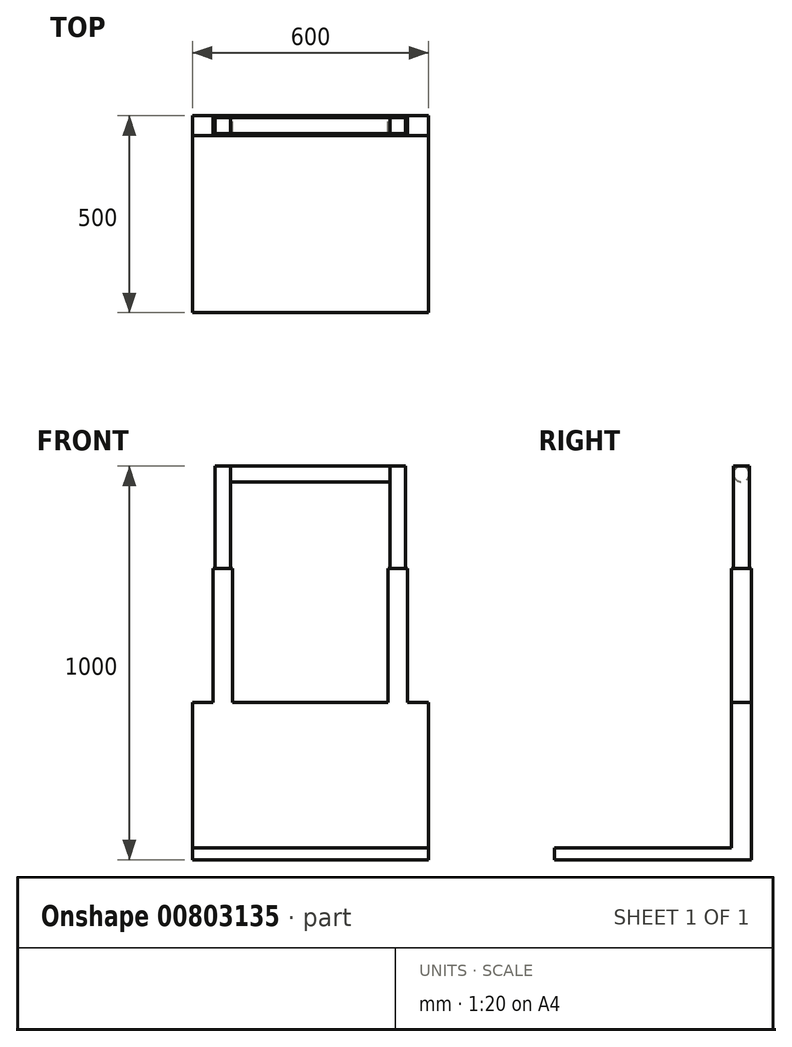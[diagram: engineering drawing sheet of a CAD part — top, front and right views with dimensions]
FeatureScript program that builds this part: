
annotation { "Feature Type Name" : "Feature", "Feature Type Description" : "" }
export const myFeature = defineFeature(function(context is Context, id is Id, definition is map)
    precondition{}
    {
        {
            var Q0;
            Q0=qCreatedBy(makeId("Right.planeOp"),FACE);
            var sketch = newSketch(context, id + "F0", { "sketchPlane" : qUnion([Q0])});
            skLineSegment(sketch, "E0.bottom", {"start": v(-3.33, 13.74) * mm, "end": v(496.67, 13.74) * mm});
            skLineSegment(sketch, "E0.top", {"start": v(-3.33, -16.26) * mm, "end": v(496.67, -16.26) * mm});
            skLineSegment(sketch, "E0.left", {"start": v(-3.33, 13.74) * mm, "end": v(-3.33, -16.26) * mm});
            skLineSegment(sketch, "E0.right", {"start": v(496.67, 13.74) * mm, "end": v(496.67, -16.26) * mm});
            skLineSegment(sketch, "E1.bottom", {"start": v(496.67, 13.74) * mm, "end": v(446.67, 13.74) * mm});
            skLineSegment(sketch, "E1.top", {"start": v(496.67, 383.74) * mm, "end": v(446.67, 383.74) * mm});
            skLineSegment(sketch, "E1.left", {"start": v(496.67, 13.74) * mm, "end": v(496.67, 383.74) * mm});
            skLineSegment(sketch, "E1.right", {"start": v(446.67, 13.74) * mm, "end": v(446.67, 383.74) * mm});
            skSolve(sketch);
        }
        {
            var Q0;
            Q0=makeQuery(id+"F0.imprint","IMPRINT",FACE,{"disambiguationData":[TD([[makeQuery(id+"F0.imprint","IMPRINT",EDGE,{"derivedFrom":sQuery(id+"F0.wireOp",EDGE,"E1.top")}),1.0]])]});
            var Q1;
            Q1=makeQuery(id+"F0.imprint","IMPRINT",FACE,{"disambiguationData":[TD([[makeQuery(id+"F0.imprint","IMPRINT",EDGE,{"derivedFrom":sQuery(id+"F0.wireOp",EDGE,"E0.top")}),1.0]])]});
            extrude(context, id + "F1", {"entities" : qUnion([Q0, Q1]), "oppositeDirection" : true, "depth" : 600 * mm, "offsetDistance" : 25 * mm});
        }
        {
            var Q0;
            Q0=makeQuery(id+"F1.opExtrude","SWEPT_FACE",FACE,{"disambiguationData":[OSD([sQuery(id+"F0.wireOp",EDGE,"E1.top")])]});
            var sketch = newSketch(context, id + "F2", { "sketchPlane" : qUnion([Q0])});
            skLineSegment(sketch, "E2.bottom", {"start": v(-547.25, 446.67) * mm, "end": v(-497.25, 446.67) * mm});
            skLineSegment(sketch, "E2.top", {"start": v(-547.25, 496.67) * mm, "end": v(-497.25, 496.67) * mm});
            skLineSegment(sketch, "E2.left", {"start": v(-547.25, 446.67) * mm, "end": v(-547.25, 496.67) * mm});
            skLineSegment(sketch, "E2.right", {"start": v(-497.25, 446.67) * mm, "end": v(-497.25, 496.67) * mm});
            skLineSegment(sketch, "E3.bottom", {"start": v(-542.25, 451.67) * mm, "end": v(-502.25, 451.67) * mm});
            skLineSegment(sketch, "E3.top", {"start": v(-542.25, 491.67) * mm, "end": v(-502.25, 491.67) * mm});
            skLineSegment(sketch, "E3.left", {"start": v(-542.25, 451.67) * mm, "end": v(-542.25, 491.67) * mm});
            skLineSegment(sketch, "E3.right", {"start": v(-502.25, 451.67) * mm, "end": v(-502.25, 491.67) * mm});
            skLineSegment(sketch, "E4", {"start": v(-300, 713.33) * mm, "end": v(-300, 248.48) * mm});
            skLineSegment(sketch, "E5.MirrorCS", {"start": v(-102.75, 446.67) * mm, "end": v(-102.75, 496.67) * mm});
            skLineSegment(sketch, "E6.MirrorCS", {"start": v(-52.75, 496.67) * mm, "end": v(-102.75, 496.67) * mm});
            skLineSegment(sketch, "E7.MirrorCS", {"start": v(-52.75, 446.67) * mm, "end": v(-52.75, 496.67) * mm});
            skLineSegment(sketch, "E8.MirrorCS", {"start": v(-52.75, 446.67) * mm, "end": v(-102.75, 446.67) * mm});
            skLineSegment(sketch, "E9.MirrorCS", {"start": v(-57.75, 451.67) * mm, "end": v(-97.75, 451.67) * mm});
            skLineSegment(sketch, "E10.MirrorCS", {"start": v(-57.75, 491.67) * mm, "end": v(-97.75, 491.67) * mm});
            skLineSegment(sketch, "E11.MirrorCS", {"start": v(-97.75, 451.67) * mm, "end": v(-97.75, 491.67) * mm});
            skLineSegment(sketch, "E12.MirrorCS", {"start": v(-57.75, 451.67) * mm, "end": v(-57.75, 491.67) * mm});
            skSolve(sketch);
        }
        {
            var Q0;
            Q0=makeQuery(id+"F2.imprint","IMPRINT",FACE,{"disambiguationData":[TD([[makeQuery(id+"F2.imprint","IMPRINT",EDGE,{"derivedFrom":sQuery(id+"F2.wireOp",EDGE,"E2.bottom")}),1.0]])]});
            extrude(context, id + "F3", {"entities" : qUnion([Q0]), "operationType" : NewBodyOperationType.ADD, "depth" : 340 * mm, "offsetDistance" : 25 * mm});
        }
        {
            var Q0;
            Q0=makeQuery(id+"F2.imprint","IMPRINT",FACE,{"disambiguationData":[TD([[makeQuery(id+"F2.imprint","IMPRINT",EDGE,{"derivedFrom":sQuery(id+"F2.wireOp",EDGE,"E5.MirrorCS")}),-1.0]])]});
            extrude(context, id + "F4", {"entities" : qUnion([Q0]), "operationType" : NewBodyOperationType.ADD, "depth" : 340 * mm, "offsetDistance" : 25 * mm});
        }
        {
            var Q0;
            Q0=makeQuery(id+"F2.imprint","IMPRINT",FACE,{"disambiguationData":[TD([[makeQuery(id+"F2.imprint","IMPRINT",EDGE,{"derivedFrom":sQuery(id+"F2.wireOp",EDGE,"E3.bottom")}),1.0]])]});
            extrude(context, id + "F5", {"entities" : qUnion([Q0]), "depth" : 600 * mm, "offsetDistance" : 25 * mm});
        }
        {
            var Q0;
            Q0=makeQuery(id+"F2.imprint","IMPRINT",FACE,{"disambiguationData":[TD([[makeQuery(id+"F2.imprint","IMPRINT",EDGE,{"derivedFrom":sQuery(id+"F2.wireOp",EDGE,"E9.MirrorCS")}),-1.0]])]});
            extrude(context, id + "F6", {"entities" : qUnion([Q0]), "operationType" : NewBodyOperationType.ADD, "depth" : 600 * mm, "offsetDistance" : 25 * mm});
        }
        {
            var Q0;
            Q0=makeQuery(id+"F5.opExtrude","SWEPT_FACE",FACE,{"disambiguationData":[OSD([sQuery(id+"F2.wireOp",EDGE,"E3.right")])]});
            var sketch = newSketch(context, id + "F7", { "sketchPlane" : qUnion([Q0])});
            skCircle(sketch, "E13", {"center": v(471.67, 963.74) * mm, "radius": 20 * mm});
            skSolve(sketch);
        }
        {
            var Q0;
            Q0 = qSketchRegion(id + "F7", true);
            extrude(context, id + "F8", {"entities" : qUnion([Q0]), "operationType" : NewBodyOperationType.ADD, "depth" : 410 * mm, "offsetDistance" : 25 * mm});
        }
    });
